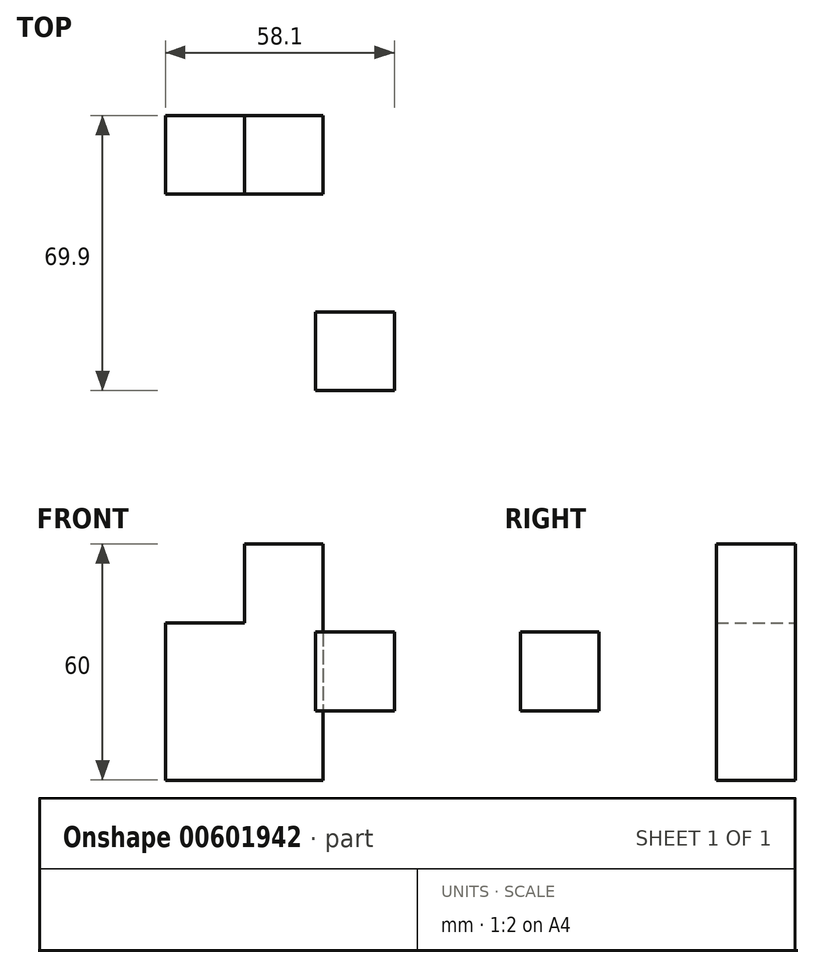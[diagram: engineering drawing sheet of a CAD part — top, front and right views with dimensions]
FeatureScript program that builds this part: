
annotation { "Feature Type Name" : "Feature", "Feature Type Description" : "" }
export const myFeature = defineFeature(function(context is Context, id is Id, definition is map)
    precondition{}
    {
        {
            var Q0;
            Q0=qCreatedBy(makeId("Front.planeOp"),FACE);
            var sketch = newSketch(context, id + "F0", { "sketchPlane" : qUnion([Q0])});
            skLineSegment(sketch, "E0", {"start": v(0, 42.37) * mm, "end": v(20, 42.37) * mm});
            skLineSegment(sketch, "E1", {"start": v(20, 42.37) * mm, "end": v(20, -17.63) * mm});
            skLineSegment(sketch, "E2", {"start": v(20, -17.63) * mm, "end": v(-20, -17.63) * mm});
            skLineSegment(sketch, "E3", {"start": v(-20, -17.63) * mm, "end": v(-20, 22.37) * mm});
            skLineSegment(sketch, "E4", {"start": v(-20, 22.37) * mm, "end": v(0, 22.37) * mm});
            skLineSegment(sketch, "E5", {"start": v(0, 22.37) * mm, "end": v(0, 42.37) * mm});
            skSolve(sketch);
        }
        {
            var Q0;
            Q0 = qSketchRegion(id + "F0", true);
            extrude(context, id + "F1", {"entities" : qUnion([Q0]), "depth" : 20 * mm, "offsetDistance" : 25 * mm});
        }
        {
            var Q0;
            Q0=qCreatedBy(makeId("Top.planeOp"),FACE);
            var sketch = newSketch(context, id + "F2", { "sketchPlane" : qUnion([Q0])});
            skLineSegment(sketch, "E6", {"start": v(18.1, -49.9) * mm, "end": v(18.1, -69.9) * mm});
            skLineSegment(sketch, "E7", {"start": v(18.1, -69.9) * mm, "end": v(38.1, -69.9) * mm});
            skLineSegment(sketch, "E8", {"start": v(38.1, -49.9) * mm, "end": v(38.1, -69.9) * mm});
            skLineSegment(sketch, "E9", {"start": v(38.1, -49.9) * mm, "end": v(18.1, -49.9) * mm});
            skSolve(sketch);
        }
        {
            var Q0;
            Q0 = qSketchRegion(id + "F2", true);
            extrude(context, id + "F3", {"entities" : qUnion([Q0]), "depth" : 20 * mm, "offsetDistance" : 25 * mm});
        }
    });
